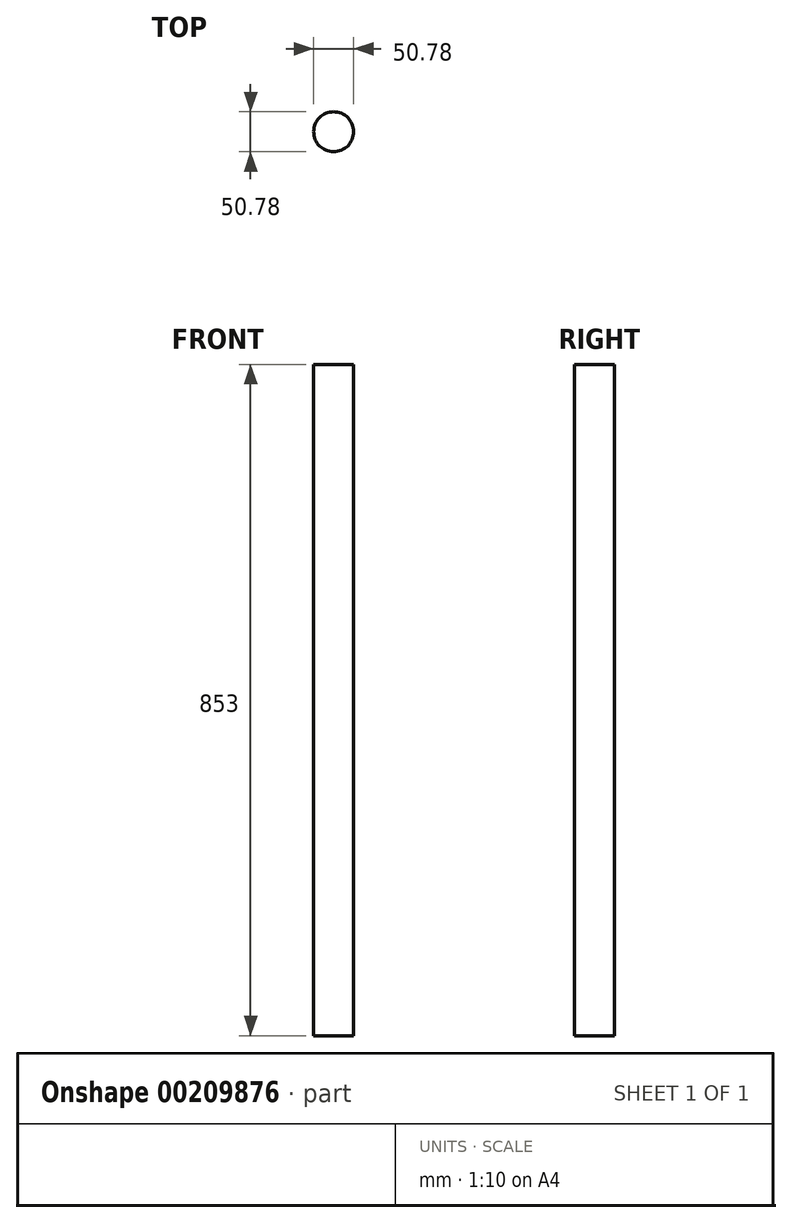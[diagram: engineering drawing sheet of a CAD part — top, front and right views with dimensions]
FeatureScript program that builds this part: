
annotation { "Feature Type Name" : "Feature", "Feature Type Description" : "" }
export const myFeature = defineFeature(function(context is Context, id is Id, definition is map)
    precondition{}
    {
        {
            var Q0;
            Q0=qCreatedBy(makeId("Top.planeOp"),FACE);
            var sketch = newSketch(context, id + "F0", { "sketchPlane" : qUnion([Q0])});
            skCircle(sketch, "E0", {"center": v(0, 0) * mm, "radius": 25.39 * mm});
            skCircle(sketch, "E1", {"center": v(104.62, -10.55) * mm, "radius": 14.73 * mm});
            skSolve(sketch);
        }
        {
            var Q0;
            Q0=makeQuery(id+"F0.imprint","IMPRINT",FACE,{"disambiguationData":[TD([[makeQuery(id+"F0.imprint","IMPRINT",EDGE,{"derivedFrom":sQuery(id+"F0.wireOp",EDGE,"E0")}),1.0]])]});
            extrude(context, id + "F1", {"entities" : qUnion([Q0]), "depth" : 853 * mm});
        }
    });
